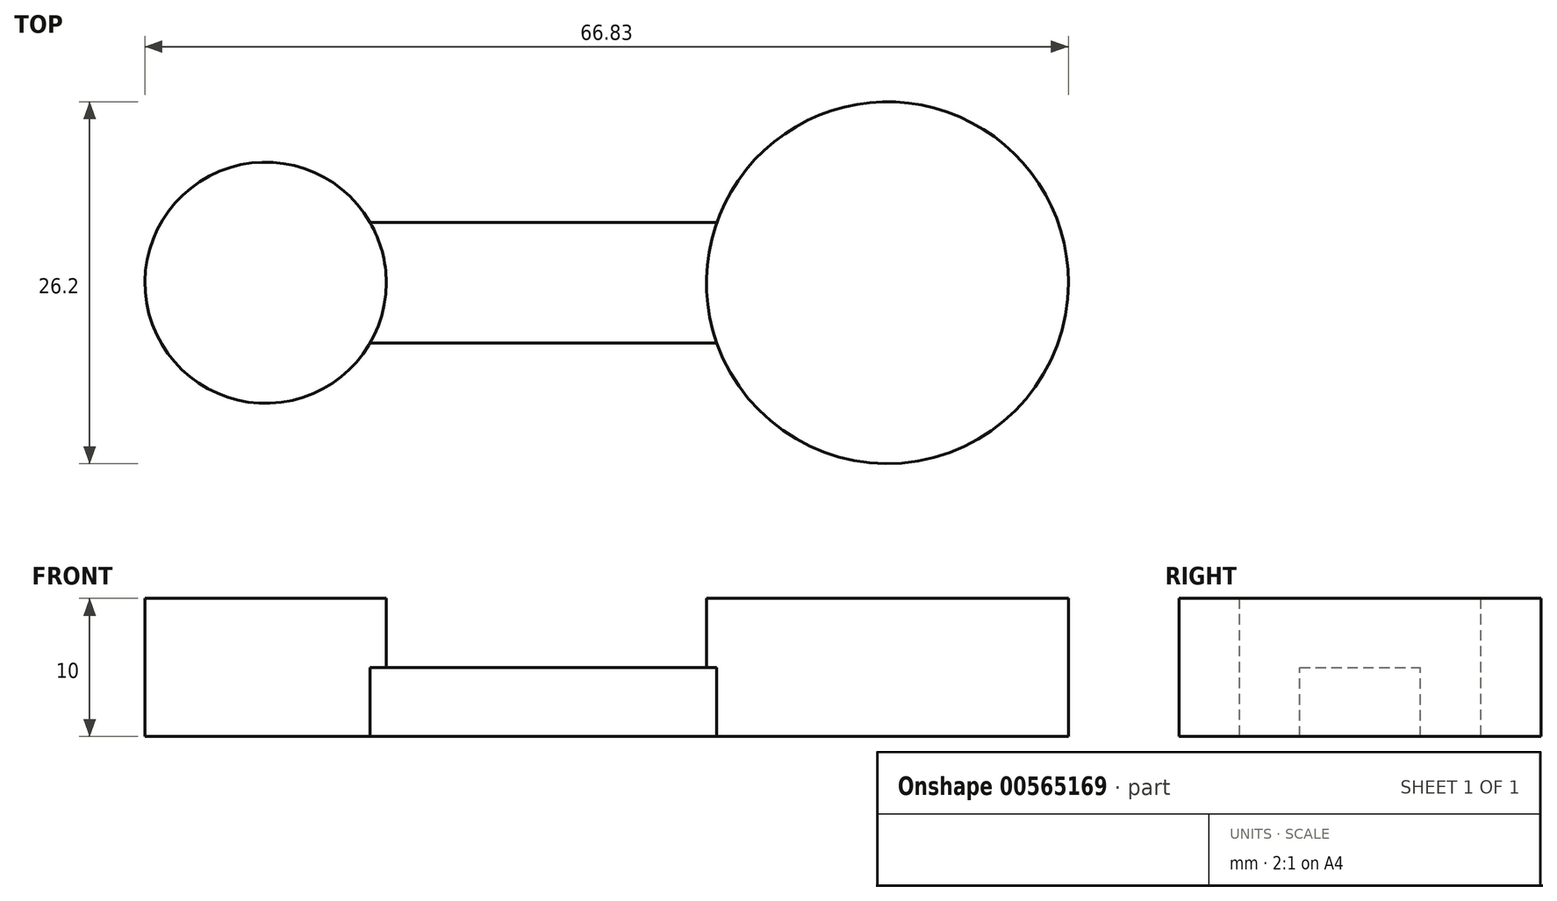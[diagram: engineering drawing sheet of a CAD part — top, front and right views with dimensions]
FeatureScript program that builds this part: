
annotation { "Feature Type Name" : "Feature", "Feature Type Description" : "" }
export const myFeature = defineFeature(function(context is Context, id is Id, definition is map)
    precondition{}
    {
        {
            assignVariable(context, id + "F0", {"name" : "W", "anyValue" : 5});
        }
        {
            var Q0;
            Q0=qCreatedBy(makeId("Top.planeOp"),FACE);
            var sketch = newSketch(context, id + "F1", { "sketchPlane" : qUnion([Q0])});
            skCircle(sketch, "E0", {"center": v(0, 0) * mm, "radius": 8.73 * mm});
            skCircle(sketch, "E1", {"center": v(45, 0) * mm, "radius": 13.1 * mm});
            skLineSegment(sketch, "E2", {"start": v(7.56, 4.37) * mm, "end": v(32.65, 4.37) * mm});
            skLineSegment(sketch, "E3", {"start": v(7.56, -4.37) * mm, "end": v(32.65, -4.37) * mm});
            skLineSegment(sketch, "E4", {"start": v(0, 0) * mm, "end": v(45, 0) * mm, "construction": true});
            skLineSegment(sketch, "E5", {"start": v(0, 0) * mm, "end": v(0, 8.73) * mm, "construction": true});
            skLineSegment(sketch, "E6", {"start": v(0, 8.73) * mm, "end": v(35.24, 8.73) * mm, "construction": true});
            skLineSegment(sketch, "E7", {"start": v(0, -8.73) * mm, "end": v(35.24, -8.73) * mm, "construction": true});
            skSolve(sketch);
        }
        {
            var Q0;
            {var subQ0=sQuery(id+"F1.wireOp",EDGE,"E0");var subQ1=makeQuery(id+"F1.imprint","INTERSECT",VERTEX,{"derivedFrom":[subQ0,sQuery(id+"F1.wireOp",EDGE,"E2")]});Q0=makeQuery(id+"F1.imprint","IMPRINT",FACE,{"disambiguationData":[TD([[makeQuery(id+"F1.imprint","IMPRINT",EDGE,{"disambiguationData":[TD([[subQ1,-1.0]])],"derivedFrom":subQ0}),1.0]])]});}
            var Q1;
            {var subQ0=sQuery(id+"F1.wireOp",EDGE,"E1");var subQ1=makeQuery(id+"F1.imprint","INTERSECT",VERTEX,{"derivedFrom":[subQ0,sQuery(id+"F1.wireOp",EDGE,"E2")]});Q1=makeQuery(id+"F1.imprint","IMPRINT",FACE,{"disambiguationData":[TD([[makeQuery(id+"F1.imprint","IMPRINT",EDGE,{"disambiguationData":[TD([[subQ1,-1.0]])],"derivedFrom":subQ0}),1.0]])]});}
            extrude(context, id + "F2", {"entities" : qUnion([Q0, Q1]), "depth" : (getVariable(context, 'W')) * mm, "offsetDistance" : 25 * mm});
        }
        {
            var Q0;
            {var subQ0=sQuery(id+"F1.wireOp",EDGE,"E1");var subQ1=makeQuery(id+"F1.imprint","INTERSECT",VERTEX,{"derivedFrom":[subQ0,sQuery(id+"F1.wireOp",EDGE,"E2")]});Q0=makeQuery(id+"F1.imprint","IMPRINT",FACE,{"disambiguationData":[TD([[makeQuery(id+"F1.imprint","IMPRINT",EDGE,{"disambiguationData":[TD([[subQ1,-1.0]])],"derivedFrom":subQ0}),1.0]])]});}
            var Q1;
            {var subQ0=sQuery(id+"F1.wireOp",EDGE,"E2");Q1=makeQuery(id+"F1.imprint","IMPRINT",FACE,{"disambiguationData":[TD([[makeQuery(id+"F1.imprint","IMPRINT",EDGE,{"derivedFrom":subQ0}),-1.0]])]});}
            var Q2;
            {var subQ0=sQuery(id+"F1.wireOp",EDGE,"E0");var subQ1=makeQuery(id+"F1.imprint","INTERSECT",VERTEX,{"derivedFrom":[subQ0,sQuery(id+"F1.wireOp",EDGE,"E2")]});Q2=makeQuery(id+"F1.imprint","IMPRINT",FACE,{"disambiguationData":[TD([[makeQuery(id+"F1.imprint","IMPRINT",EDGE,{"disambiguationData":[TD([[subQ1,-1.0]])],"derivedFrom":subQ0}),1.0]])]});}
            extrude(context, id + "F3", {"entities" : qUnion([Q0, Q1, Q2]), "operationType" : NewBodyOperationType.ADD, "oppositeDirection" : true, "depth" : (getVariable(context, 'W')) * mm, "offsetDistance" : 25 * mm});
        }
        {
            var Q0;
            Q0=makeQuery(id+"F2.opExtrude","SWEPT_BODY",BODY,{"disambiguationData":[OSD([sQuery(id+"F1.wireOp",EDGE,"E0")])]});
            transform(context, id + "F4", {"entities" : qUnion([Q0]), "transformType" : TransformType.TRANSLATION_3D, "dx" : 0 * mm, "dy" : 0 * mm, "dz" : -(getVariable(context, 'W')) * mm, "makeCopy" : false});
        }
    });
